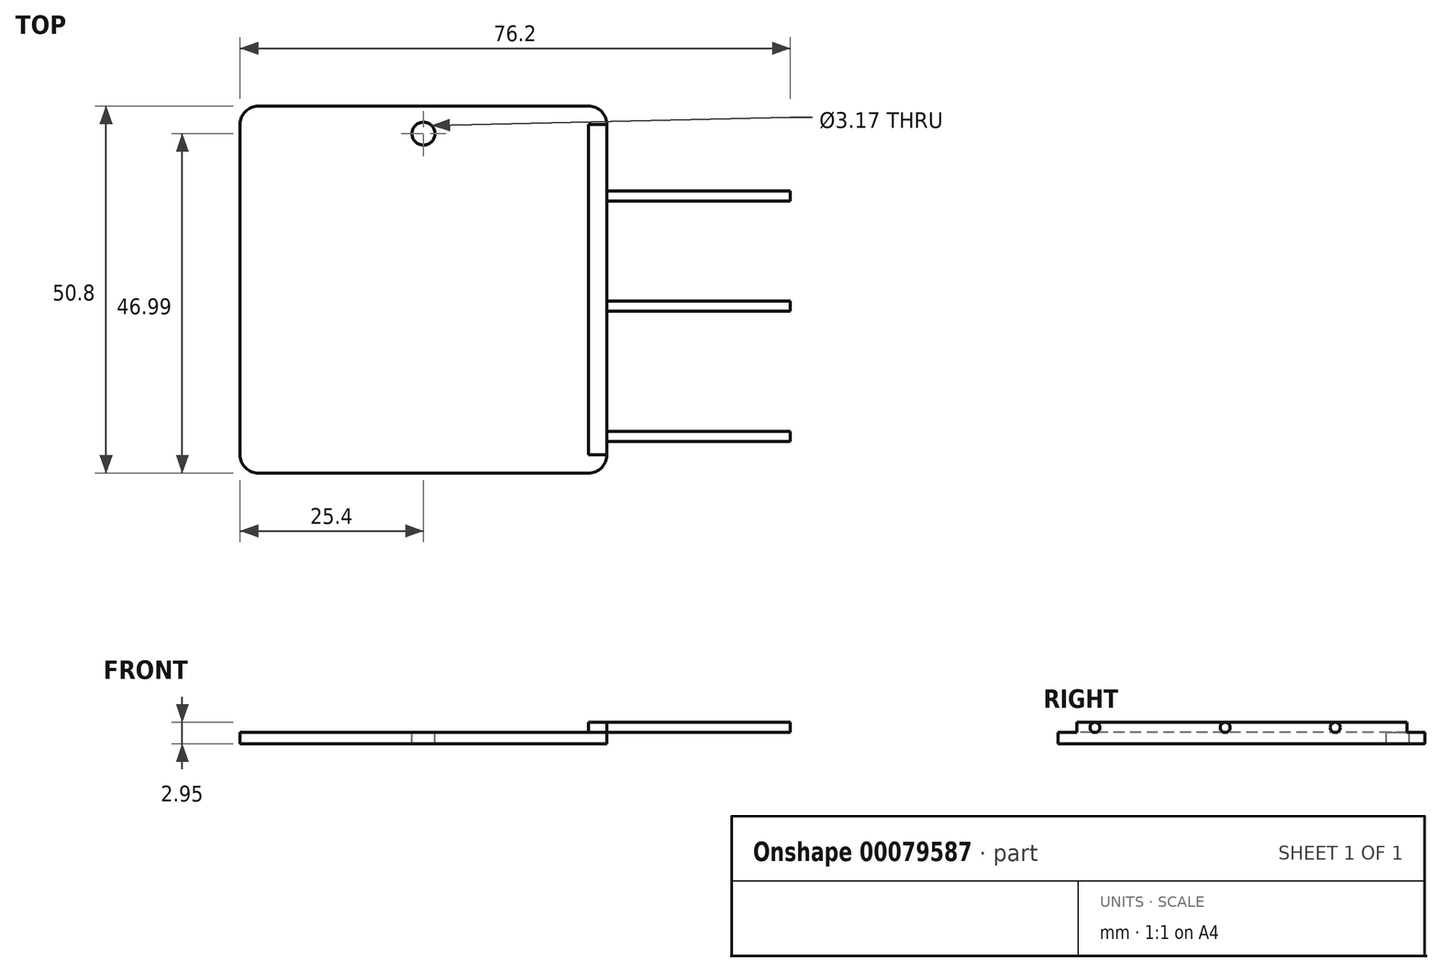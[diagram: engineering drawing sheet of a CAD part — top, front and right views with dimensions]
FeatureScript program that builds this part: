
annotation { "Feature Type Name" : "Feature", "Feature Type Description" : "" }
export const myFeature = defineFeature(function(context is Context, id is Id, definition is map)
    precondition{}
    {
        {
            var Q0;
            Q0=qCreatedBy(makeId("Top.planeOp"),FACE);
            var sketch = newSketch(context, id + "F0", { "sketchPlane" : qUnion([Q0])});
            skLineSegment(sketch, "E0.bottom", {"start": v(2.54, 0) * mm, "end": v(48.26, 0) * mm});
            skLineSegment(sketch, "E0.top", {"start": v(2.54, 50.8) * mm, "end": v(48.26, 50.8) * mm});
            skLineSegment(sketch, "E0.left", {"start": v(0, 2.54) * mm, "end": v(0, 48.26) * mm});
            skLineSegment(sketch, "E0.right", {"start": v(50.8, 2.54) * mm, "end": v(50.8, 48.26) * mm});
            skPoint(sketch, "E1.visualSharp", {"position": v(0, 50.8) * mm});
            skArc(sketch, "E1.filletArc", {"start": v(2.54, 50.8) * mm, "mid": v(0.74, 50.06) * mm, "end": v(0, 48.26) * mm});
            skPoint(sketch, "E2.visualSharp", {"position": v(50.8, 50.8) * mm});
            skArc(sketch, "E2.filletArc", {"start": v(50.8, 48.26) * mm, "mid": v(50.06, 50.06) * mm, "end": v(48.26, 50.8) * mm});
            skPoint(sketch, "E3.visualSharp", {"position": v(50.8, 0) * mm});
            skArc(sketch, "E3.filletArc", {"start": v(48.26, 0) * mm, "mid": v(50.06, 0.74) * mm, "end": v(50.8, 2.54) * mm});
            skPoint(sketch, "E4.visualSharp", {"position": v(0, 0) * mm});
            skArc(sketch, "E4.filletArc", {"start": v(0, 2.54) * mm, "mid": v(0.74, 0.74) * mm, "end": v(2.54, 0) * mm});
            skSolve(sketch);
        }
        {
            var Q0;
            Q0=makeQuery(id+"F0.imprint","IMPRINT",FACE,{"disambiguationData":[TD([[makeQuery(id+"F0.imprint","IMPRINT",EDGE,{"derivedFrom":sQuery(id+"F0.wireOp",EDGE,"E0.bottom")}),1.0]])]});
            extrude(context, id + "F1", {"entities" : qUnion([Q0]), "depth" : 1.55 * mm});
        }
        {
            var Q0;
            Q0=makeQuery(id+"F1.opExtrude","CAP_FACE",FACE,{"disambiguationData":[OSD([sQuery(id+"F0.wireOp",EDGE,"E0.bottom"),sQuery(id+"F0.wireOp",EDGE,"E0.top"),sQuery(id+"F0.wireOp",EDGE,"E0.left"),sQuery(id+"F0.wireOp",EDGE,"E0.right"),sQuery(id+"F0.wireOp",EDGE,"E1.filletArc"),sQuery(id+"F0.wireOp",EDGE,"E2.filletArc"),sQuery(id+"F0.wireOp",EDGE,"E3.filletArc"),sQuery(id+"F0.wireOp",EDGE,"E4.filletArc")])],"isStart":false});
            var sketch = newSketch(context, id + "F2", { "sketchPlane" : qUnion([Q0])});
            skCircle(sketch, "E5", {"center": v(25.4, 47) * mm, "radius": 1.59 * mm});
            skSolve(sketch);
        }
        {
            var Q0;
            Q0=makeQuery(id+"F2.imprint","IMPRINT",FACE,{"disambiguationData":[TD([[makeQuery(id+"F2.imprint","IMPRINT",EDGE,{"derivedFrom":sQuery(id+"F2.wireOp",EDGE,"E5")}),1.0]])]});
            var Q1;
            Q1=makeQuery(id+"F2.imprint","IMPRINT",FACE,{"disambiguationData":[TD([[makeQuery(id+"F2.imprint","IMPRINT",EDGE,{"derivedFrom":sQuery(id+"F2.wireOp",EDGE,"8UeJ27dL-iYED-ihap-6YzF-YeFpti1OHJYd")}),1.0]])]});
            extrude(context, id + "F3", {"entities" : qUnion([Q0, Q1]), "operationType" : NewBodyOperationType.REMOVE, "oppositeDirection" : true, "depth" : 25.4 * mm});
        }
        {
            var Q0;
            Q0=makeQuery(id+"F1.opExtrude","SWEPT_FACE",FACE,{"disambiguationData":[OSD([sQuery(id+"F0.wireOp",EDGE,"E0.right")])]});
            var sketch = newSketch(context, id + "F4", { "sketchPlane" : qUnion([Q0])});
            skCircle(sketch, "E6", {"center": v(5.08, 2.25) * mm, "radius": 0.7 * mm});
            skCircle(sketch, "E7", {"center": v(23.11, 2.25) * mm, "radius": 0.7 * mm});
            skCircle(sketch, "E8", {"center": v(38.35, 2.25) * mm, "radius": 0.7 * mm});
            skSolve(sketch);
        }
        {
            var Q0;
            Q0=makeQuery(id+"F1.opExtrude","CAP_FACE",FACE,{"disambiguationData":[OSD([sQuery(id+"F0.wireOp",EDGE,"E0.bottom"),sQuery(id+"F0.wireOp",EDGE,"E0.top"),sQuery(id+"F0.wireOp",EDGE,"E0.left"),sQuery(id+"F0.wireOp",EDGE,"E0.right"),sQuery(id+"F0.wireOp",EDGE,"E1.filletArc"),sQuery(id+"F0.wireOp",EDGE,"E2.filletArc"),sQuery(id+"F0.wireOp",EDGE,"E3.filletArc"),sQuery(id+"F0.wireOp",EDGE,"E4.filletArc")])],"isStart":false});
            var sketch = newSketch(context, id + "F5", { "sketchPlane" : qUnion([Q0])});
            skLineSegment(sketch, "E9.bottom", {"start": v(50.8, 48.26) * mm, "end": v(48.26, 48.26) * mm});
            skLineSegment(sketch, "E9.top", {"start": v(50.8, 2.54) * mm, "end": v(48.26, 2.54) * mm});
            skLineSegment(sketch, "E9.left", {"start": v(50.8, 48.26) * mm, "end": v(50.8, 2.54) * mm});
            skLineSegment(sketch, "E9.right", {"start": v(48.26, 48.26) * mm, "end": v(48.26, 2.54) * mm});
            skSolve(sketch);
        }
        {
            var Q0;
            Q0=makeQuery(id+"F5.imprint","IMPRINT",FACE,{"disambiguationData":[TD([[makeQuery(id+"F5.imprint","IMPRINT",EDGE,{"derivedFrom":sQuery(id+"F5.wireOp",EDGE,"E9.bottom")}),1.0]])]});
            extrude(context, id + "F6", {"entities" : qUnion([Q0]), "operationType" : NewBodyOperationType.ADD, "depth" : 1.4 * mm});
        }
        {
            var Q0;
            Q0=makeQuery(id+"F4.imprint","IMPRINT",FACE,{"disambiguationData":[TD([[makeQuery(id+"F4.imprint","IMPRINT",EDGE,{"derivedFrom":sQuery(id+"F4.wireOp",EDGE,"E6")}),1.0]])]});
            var Q1;
            Q1=makeQuery(id+"F4.imprint","IMPRINT",FACE,{"disambiguationData":[TD([[makeQuery(id+"F4.imprint","IMPRINT",EDGE,{"derivedFrom":sQuery(id+"F4.wireOp",EDGE,"E7")}),1.0]])]});
            var Q2;
            Q2=makeQuery(id+"F4.imprint","IMPRINT",FACE,{"disambiguationData":[TD([[makeQuery(id+"F4.imprint","IMPRINT",EDGE,{"derivedFrom":sQuery(id+"F4.wireOp",EDGE,"E8")}),1.0]])]});
            extrude(context, id + "F7", {"entities" : qUnion([Q0, Q1, Q2]), "operationType" : NewBodyOperationType.ADD, "depth" : 25.4 * mm});
        }
    });
